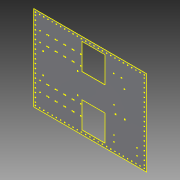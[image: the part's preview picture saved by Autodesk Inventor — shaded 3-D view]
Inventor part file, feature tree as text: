
AUTODESK INVENTOR PART (.ipt)
format: ipt  version: 2014 SP1 (Build 180222100, 222)  size: 407,040 bytes
history: native  units: in
note: dims shown in document units (in); Inventor stores cm internally (conversion verified against a paired STEP export)
features: reference x39, sketch x6, other x5, pattern_linear x2, sheet_metal_op x1
ambient origin geometry x8: Origin, YZ Plane, XZ Plane, XY Plane, X Axis, Y Axis, Z Axis, Center Point
bodies: Solid1 (feature_tree)
feature tree (53):
  sheet_metal_op  "Face1"
  pattern_linear  "Rectangular Pattern2"  Spacing1=0.0625in  [1 undecoded]
  pattern_linear  "Rectangular Pattern5"  Spacing1=0.0in  [1 undecoded]
  sketch  "Sketch17"  dims[d6=7.25in d17=0.0625in d18=0.0in d19=10.6299in d21=1.0in d23=1.0in d24=1.0in d65=0.0625in d66=0.0in d78=11.55in d79=5.5in d80=11.55in d97=0.0625in d98=0.0in d99=7.4803in d101=1.0in d102=0.7874in d104=26.0in d105=0.0625in d106=0.0in]
  sketch  "Sketch1"  dims[d0=27.0in]
  other  "Plate1"
  sketch  "Sketch2"  dims[d1=20.325in]
  sketch  "Sketch4"  dims[d2=0.0625in]
  reference  "Reference4"
  reference  "Reference5"
  sketch  "Sketch12"  dims[d4=7.25in]
  reference  "Reference10"
  reference  "Reference11"
  sketch  "Sketch16"  dims[d5=5.5in]
  reference  "Reference12"
  reference  "Reference13"
  reference  "Reference14"
  reference  "Reference15"
  reference  "Reference16"
  reference  "Reference17"
  reference  "Reference18"
  reference  "Reference19"
  reference  "Reference20"
  reference  "Reference21"
  reference  "Reference22"
  reference  "Reference23"
  reference  "Reference24"
  reference  "Reference25"
  reference  "Reference26"
  reference  "Reference27"
  reference  "Reference28"
  reference  "Reference29"
  reference  "Reference30"
  reference  "Reference31"
  reference  "Reference32"
  reference  "Reference33"
  reference  "Reference34"
  reference  "Reference35"
  reference  "Reference36"
  reference  "Reference37"
  reference  "Reference38"
  reference  "Reference39"
  reference  "Reference40"
  reference  "Reference41"
  reference  "Reference42"
  reference  "Reference43"
  reference  "Reference44"
  reference  "Reference45"
  reference  "Reference46"
  other  "Cut3"
  other  "Cut6"
  other  "Cut8"
  other  "Cut9"
note: 2 required parameter values undecoded (feature->parameter linkage not recoverable at this tier; creation-order binding heuristic only, values carry confidence <= 0.55)
